# Revit family: Hat_Coat_Rack-Bradley_Corp-Stainless-994x
name_source: partatom
category: Specialty Equipment
revit_build: Autodesk Revit MEP 2012 (Build: 20110309_2315(x64)
units: mm (PartAtom-declared; Revit-internal decimal feet)

## types (4) — shared parameters
ADA Compliant = No
Accessory Material = Metal - Bradley Corp - Stainless Steel-Satin
Assembly Code = C1030200
Buy American Act = To Be Determined
Cold Water Connection Diameter = 0"
Default Elevation = 48"
Depth = 0"
Height = 0"
Hot Water Connection Diameter = 0"
Installation Type = Wall Mounted
Length = 0"
Low Emitting Material = No
Manufacturer = Bradley Corporation
MasterFormat Number = 10 57 13
MasterFormat Title = Hat and Coat Racks
OmniClass Code = 23-21 15 17
OmniClass Title = Clothing Racks
Product Tech Data URL - English = http://bradleycorp.com
Product Tech Data URL - French = http://bradleycorp.com
Product Tech Data URL - Spanish = http://bradleycorp.com
Specifications URL = http://www.bradleycorp.com
URL = http://www.bradleycorp.com
Version = 2.0
Waste Water Connection Diameter = 0"
Width = 0"
zero-valued in all types: Percentage of Recycled Content

## per-type parameters (varying)
| type | DIM A | DIM B | DIM C | Description |
| 9946 | 60" | 10 3/4" | 3 1/4" | Hat & Coat Rack w/6 Hooks 60" W |
| 9945 | 48" | 11" | 2" | Hat & Coat Rack w/5 Hooks 48" W |
| 9943 BradEX | 24" | 9" | 3" | Hat & Coat Rack w/3 Hooks 24" W |
| 9944 | 36" | 10" | 3" | Hat & Coat Rack w/4 Hooks 36" W |

note: column(s) folded — value = type name in every type: Model

## geometry (parser evidence)
native form markers: Blend x6, Sweep x3
no freeform markers — native parametric forms only
